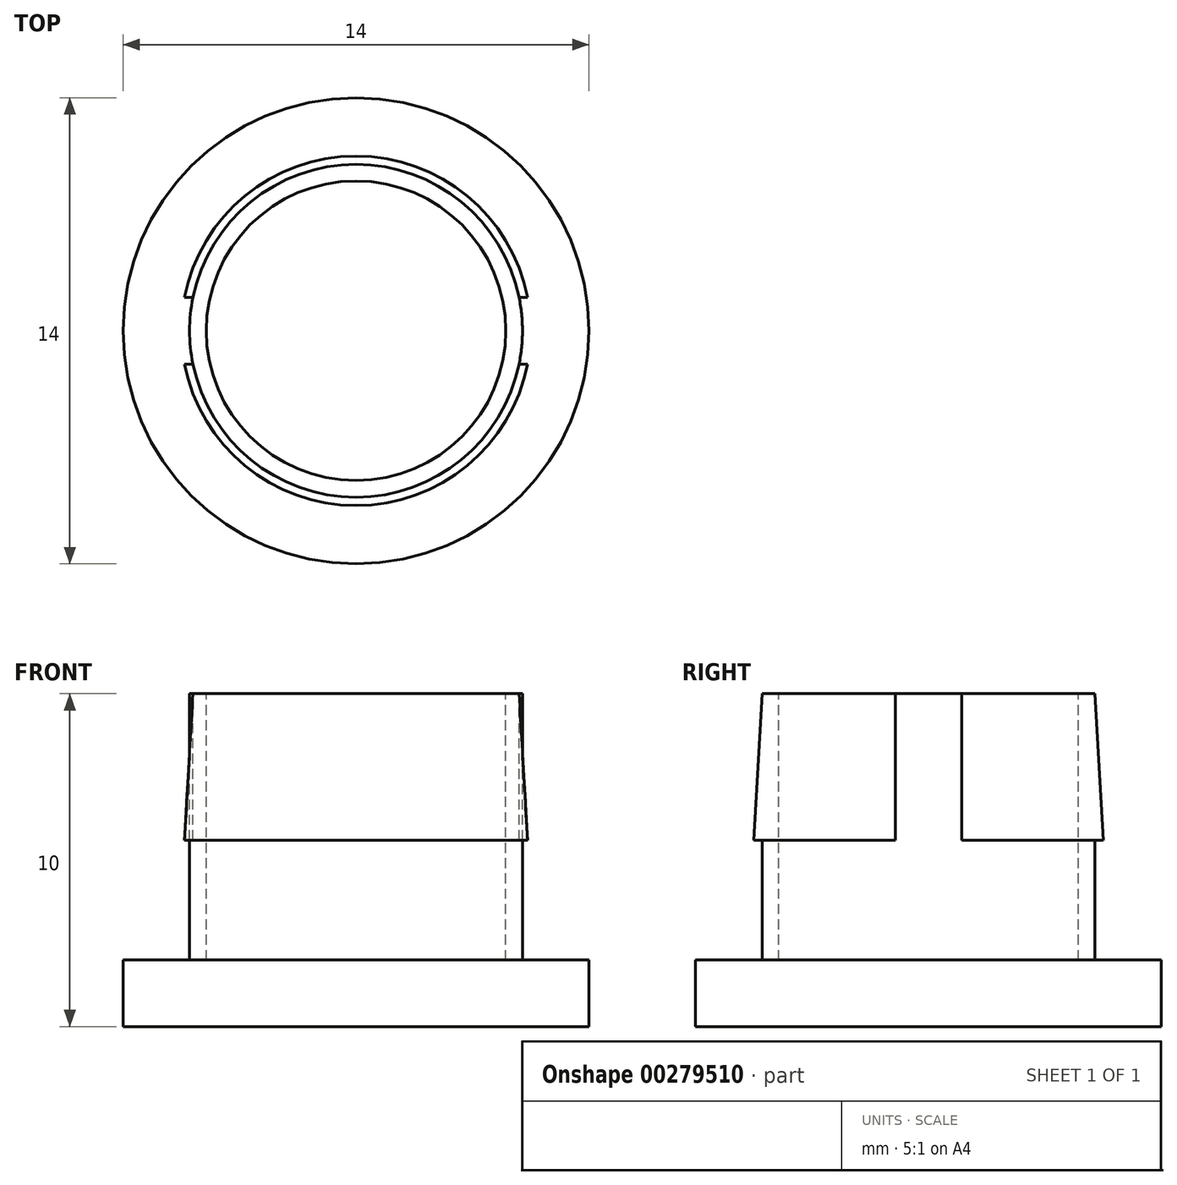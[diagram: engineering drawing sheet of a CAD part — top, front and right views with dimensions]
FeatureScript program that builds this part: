
annotation { "Feature Type Name" : "Feature", "Feature Type Description" : "" }
export const myFeature = defineFeature(function(context is Context, id is Id, definition is map)
    precondition{}
    {
        {
            var Q0;
            Q0=qCreatedBy(makeId("Front.planeOp"),FACE);
            var sketch = newSketch(context, id + "F0", { "sketchPlane" : qUnion([Q0])});
            skLineSegment(sketch, "E0", {"start": v(0, 0) * mm, "end": v(-7, 0) * mm});
            skLineSegment(sketch, "E1", {"start": v(-7, 0) * mm, "end": v(-7, 2) * mm});
            skLineSegment(sketch, "E2", {"start": v(-7, 2) * mm, "end": v(-5, 2) * mm});
            skLineSegment(sketch, "E3", {"start": v(-5, 2) * mm, "end": v(-5, 5.6) * mm});
            skLineSegment(sketch, "E4", {"start": v(-5, 5.6) * mm, "end": v(-5.25, 5.6) * mm});
            skLineSegment(sketch, "E5", {"start": v(-5.25, 5.6) * mm, "end": v(-5, 10) * mm});
            skLineSegment(sketch, "E6", {"start": v(-5, 10) * mm, "end": v(0, 10) * mm});
            skLineSegment(sketch, "E7", {"start": v(0, 10) * mm, "end": v(0, 0) * mm});
            skSolve(sketch);
        }
        {
            var Q0;
            Q0=makeQuery(id+"F0.imprint","IMPRINT",FACE,{"disambiguationData":[TD([[makeQuery(id+"F0.imprint","IMPRINT",EDGE,{"derivedFrom":sQuery(id+"F0.wireOp",EDGE,"E0")}),-1.0]])]});
            var Q1;
            Q1=sQuery(id+"F0.wireOp",EDGE,"E7");
            revolve(context, id + "F1", {"entities" : qUnion([Q0]), "axis" : qUnion([Q1]), "revolveType" : RevolveType.FULL});
        }
        {
            var Q0;
            Q0=makeQuery(id+"F1.opRevolve","SWEPT_FACE",FACE,{"disambiguationData":[OSD([sQuery(id+"F0.wireOp",EDGE,"E6")])]});
            var sketch = newSketch(context, id + "F2", { "sketchPlane" : qUnion([Q0])});
            skCircle(sketch, "E8", {"center": v(0, 0) * mm, "radius": 4.5 * mm});
            skSolve(sketch);
        }
        {
            var Q0;
            Q0 = qSketchRegion(id + "F2", true);
            extrude(context, id + "F3", {"entities" : qUnion([Q0]), "operationType" : NewBodyOperationType.REMOVE, "oppositeDirection" : true, "depth" : 8 * mm});
        }
        {
            var Q0;
            Q0=makeQuery(id+"F1.opRevolve","SWEPT_FACE",FACE,{"disambiguationData":[OSD([sQuery(id+"F0.wireOp",EDGE,"E6")])]});
            var sketch = newSketch(context, id + "F4", { "sketchPlane" : qUnion([Q0])});
            skLineSegment(sketch, "E9.bottom", {"start": v(15.86, 1) * mm, "end": v(-14.14, 1) * mm});
            skLineSegment(sketch, "E9.top", {"start": v(15.86, -1) * mm, "end": v(-14.14, -1) * mm});
            skLineSegment(sketch, "E9.left", {"start": v(15.86, 1) * mm, "end": v(15.86, -1) * mm});
            skLineSegment(sketch, "E9.right", {"start": v(-14.14, 1) * mm, "end": v(-14.14, -1) * mm});
            skSolve(sketch);
        }
        {
            var Q0;
            {var subQ0=sQuery(id+"F4.wireOp",EDGE,"E9.right");Q0=makeQuery(id+"F4.imprint","IMPRINT",FACE,{"disambiguationData":[TD([[makeQuery(id+"F4.imprint","IMPRINT",EDGE,{"derivedFrom":subQ0}),1.0]])]});}
            var Q1;
            {var subQ0=sQuery(id+"F4.wireOp",EDGE,"E9.bottom");var subQ3=makeQuery(id+"F3.boolean.opBoolean","COPY",EDGE,{"derivedFrom":makeQuery(id+"F3.opExtrude","CAP_EDGE",EDGE,{"disambiguationData":[OSD([sQuery(id+"F2.wireOp",EDGE,"E8")])],"isStart":true})});var subQ4=makeQuery(id+"F4.imprint","INTERSECT",VERTEX,{"disambiguationData":[OD(1.0)],"derivedFrom":[subQ3,subQ0]});Q1=makeQuery(id+"F4.imprint","IMPRINT",FACE,{"disambiguationData":[TD([[makeQuery(id+"F4.imprint","IMPRINT",EDGE,{"disambiguationData":[TD([[subQ4,-1.0]])],"derivedFrom":subQ3}),-1.0]])]});}
            var Q2;
            {var subQ0=sQuery(id+"F4.wireOp",EDGE,"E9.bottom");var subQ3=makeQuery(id+"F3.boolean.opBoolean","COPY",EDGE,{"derivedFrom":makeQuery(id+"F3.opExtrude","CAP_EDGE",EDGE,{"disambiguationData":[OSD([sQuery(id+"F2.wireOp",EDGE,"E8")])],"isStart":true})});var subQ4=makeQuery(id+"F4.imprint","INTERSECT",VERTEX,{"disambiguationData":[OD(0.0)],"derivedFrom":[subQ3,subQ0]});Q2=makeQuery(id+"F4.imprint","IMPRINT",FACE,{"disambiguationData":[TD([[makeQuery(id+"F4.imprint","IMPRINT",EDGE,{"disambiguationData":[TD([[subQ4,1.0]])],"derivedFrom":subQ3}),-1.0]])]});}
            var Q3;
            {var subQ0=sQuery(id+"F4.wireOp",EDGE,"E9.left");Q3=makeQuery(id+"F4.imprint","IMPRINT",FACE,{"disambiguationData":[TD([[makeQuery(id+"F4.imprint","IMPRINT",EDGE,{"derivedFrom":subQ0}),-1.0]])]});}
            extrude(context, id + "F5", {"entities" : qUnion([Q0, Q1, Q2, Q3]), "operationType" : NewBodyOperationType.REMOVE, "oppositeDirection" : true, "depth" : 4.4 * mm});
        }
    });
